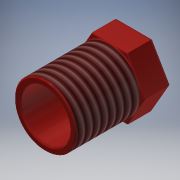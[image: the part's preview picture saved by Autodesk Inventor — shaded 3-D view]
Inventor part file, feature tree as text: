
AUTODESK INVENTOR PART (.ipt)
format: ipt  version: 2018 (Build 220112000, 112)  size: 537,088 bytes
history: native  units: mm
features: thread x1
ambient origin geometry x8: Origin, YZ Plane, XZ Plane, XY Plane, X Axis, Y Axis, Z Axis, Center Point
bodies: Solid2 (feature_tree), Solid1 (feature_tree)
feature tree (1):
  thread  "Thread1"  [1 undecoded]
note: 1 required parameter value undecoded (feature->parameter linkage not recoverable at this tier; creation-order binding heuristic only, values carry confidence <= 0.55)
